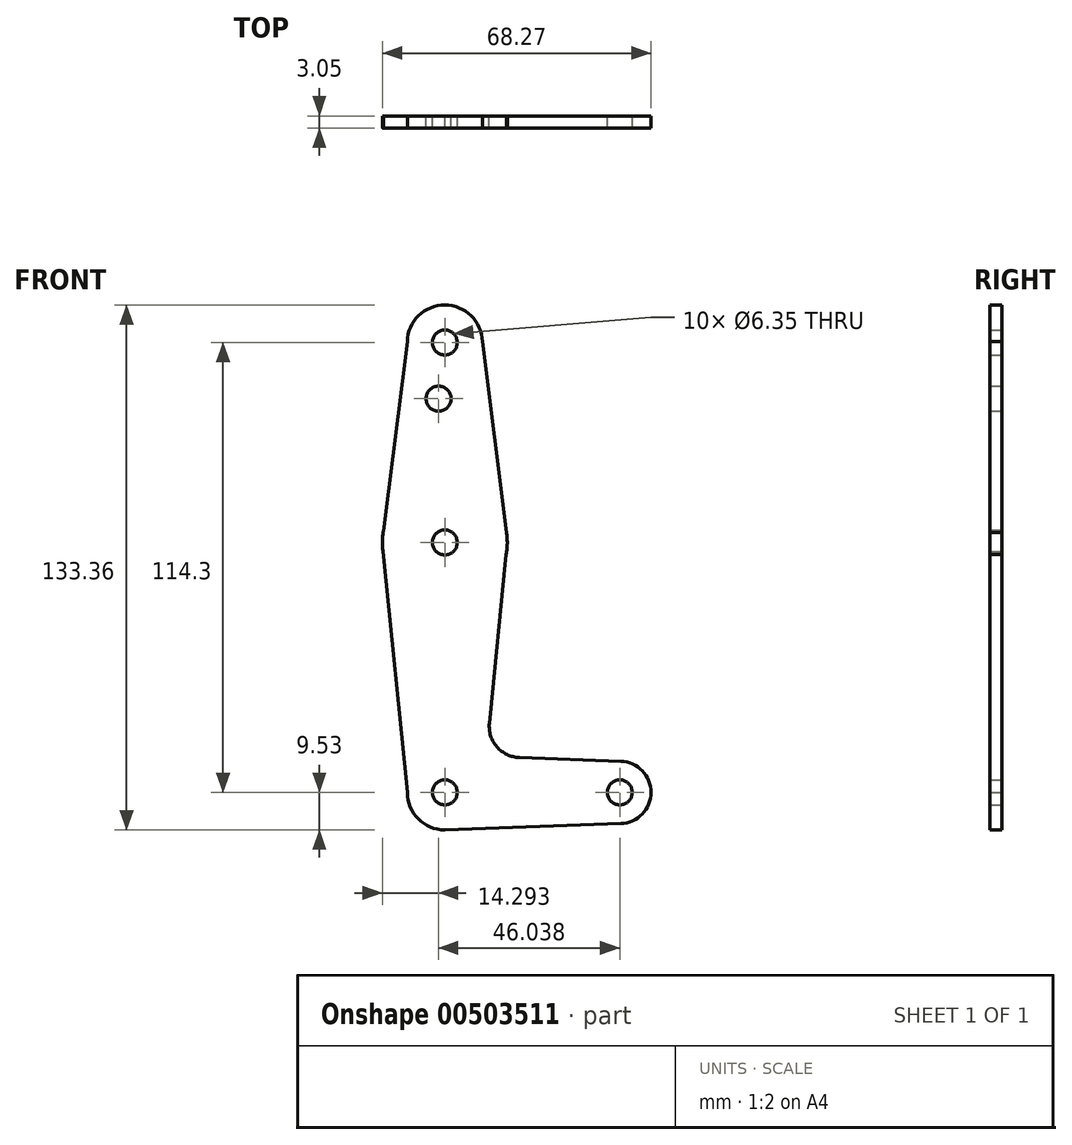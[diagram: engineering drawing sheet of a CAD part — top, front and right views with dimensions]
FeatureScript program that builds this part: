
annotation { "Feature Type Name" : "Feature", "Feature Type Description" : "" }
export const myFeature = defineFeature(function(context is Context, id is Id, definition is map)
    precondition{}
    {
        {
            var Q0;
            Q0=qCreatedBy(makeId("Front.planeOp"),FACE);
            var sketch = newSketch(context, id + "F0", { "sketchPlane" : qUnion([Q0])});
            skLineSegment(sketch, "E0", {"start": v(0, 0) * mm, "end": v(0, 63.5) * mm, "construction": true});
            skLineSegment(sketch, "E1", {"start": v(0, 63.5) * mm, "end": v(0, 114.3) * mm, "construction": true});
            skLineSegment(sketch, "E2", {"start": v(0, 0) * mm, "end": v(44.45, 0) * mm, "construction": true});
            skCircle(sketch, "E3", {"center": v(0, 114.3) * mm, "radius": 9.53 * mm});
            skCircle(sketch, "E4", {"center": v(0, 63.5) * mm, "radius": 15.88 * mm});
            skCircle(sketch, "E5", {"center": v(0, 0) * mm, "radius": 9.53 * mm});
            skCircle(sketch, "E6", {"center": v(44.45, 0) * mm, "radius": 7.94 * mm});
            skLineSegment(sketch, "E7", {"start": v(-9.52, 114.53) * mm, "end": v(-15.6, 66.45) * mm});
            skLineSegment(sketch, "E8", {"start": v(9.52, 114.53) * mm, "end": v(15.66, 66.08) * mm});
            skLineSegment(sketch, "E9", {"start": v(-9.53, 0) * mm, "end": v(-15.7, 61.16) * mm});
            skLineSegment(sketch, "E10", {"start": v(15.6, 60.51) * mm, "end": v(11.32, 17.58) * mm});
            skLineSegment(sketch, "E11", {"start": v(0, -9.53) * mm, "end": v(44.73, -7.93) * mm});
            skLineSegment(sketch, "E12", {"start": v(18.95, 8.85) * mm, "end": v(44.73, 7.93) * mm});
            skCircle(sketch, "E13", {"center": v(0, 114.3) * mm, "radius": 3.18 * mm});
            skCircle(sketch, "E14", {"center": v(0, 63.5) * mm, "radius": 3.18 * mm});
            skCircle(sketch, "E15", {"center": v(0, 0) * mm, "radius": 3.18 * mm});
            skCircle(sketch, "E16", {"center": v(44.45, 0) * mm, "radius": 3.18 * mm});
            skCircle(sketch, "E17", {"center": v(-1.59, 100.03) * mm, "radius": 3.18 * mm});
            skPoint(sketch, "E18.newPointA", {"position": v(0, 9.53) * mm});
            skArc(sketch, "E18.filletArc", {"start": v(11.32, 17.58) * mm, "mid": v(13.24, 11.57) * mm, "end": v(18.95, 8.85) * mm});
            skSolve(sketch);
        }
        {
            var Q0;
            {var subQ0=sQuery(id+"F0.wireOp",EDGE,"E11");var subQ1=sQuery(id+"F0.wireOp",EDGE,"E5");var subQ2=makeQuery(id+"F0.imprint","INTERSECT",VERTEX,{"disambiguationData":[OD(0.0)],"derivedFrom":[subQ1,subQ0]});Q0=makeQuery(id+"F0.imprint","IMPRINT",FACE,{"disambiguationData":[TD([[makeQuery(id+"F0.imprint","IMPRINT",EDGE,{"disambiguationData":[TD([[subQ2,-1.0]])],"derivedFrom":subQ1}),1.0]])]});}
            var Q1;
            Q1=makeQuery(id+"F0.imprint","IMPRINT",FACE,{"disambiguationData":[TD([[makeQuery(id+"F0.imprint","IMPRINT",EDGE,{"derivedFrom":sQuery(id+"F0.wireOp",EDGE,"E13")}),-1.0]])]});
            var Q2;
            Q2=makeQuery(id+"F0.imprint","IMPRINT",FACE,{"disambiguationData":[TD([[makeQuery(id+"F0.imprint","IMPRINT",EDGE,{"derivedFrom":sQuery(id+"F0.wireOp",EDGE,"E16")}),-1.0]])]});
            var Q3;
            Q3=makeQuery(id+"F0.imprint","IMPRINT",FACE,{"disambiguationData":[TD([[makeQuery(id+"F0.imprint","IMPRINT",EDGE,{"derivedFrom":sQuery(id+"F0.wireOp",EDGE,"E14")}),-1.0]])]});
            var Q4;
            {var subQ0=sQuery(id+"F0.wireOp",EDGE,"E9");Q4=makeQuery(id+"F0.imprint","IMPRINT",FACE,{"disambiguationData":[TD([[makeQuery(id+"F0.imprint","IMPRINT",EDGE,{"derivedFrom":subQ0}),-1.0]])]});}
            var Q5;
            Q5=makeQuery(id+"F0.imprint","IMPRINT",FACE,{"disambiguationData":[TD([[makeQuery(id+"F0.imprint","IMPRINT",EDGE,{"derivedFrom":sQuery(id+"F0.wireOp",EDGE,"E15")}),-1.0]])]});
            var Q6;
            {var subQ1=sQuery(id+"F0.wireOp",EDGE,"E7");Q6=makeQuery(id+"F0.imprint","IMPRINT",FACE,{"disambiguationData":[TD([[makeQuery(id+"F0.imprint","IMPRINT",EDGE,{"derivedFrom":subQ1}),1.0]])]});}
            extrude(context, id + "F1", {"entities" : qUnion([Q0, Q1, Q2, Q3, Q4, Q5, Q6]), "depth" : 3.05 * mm});
        }
    });
